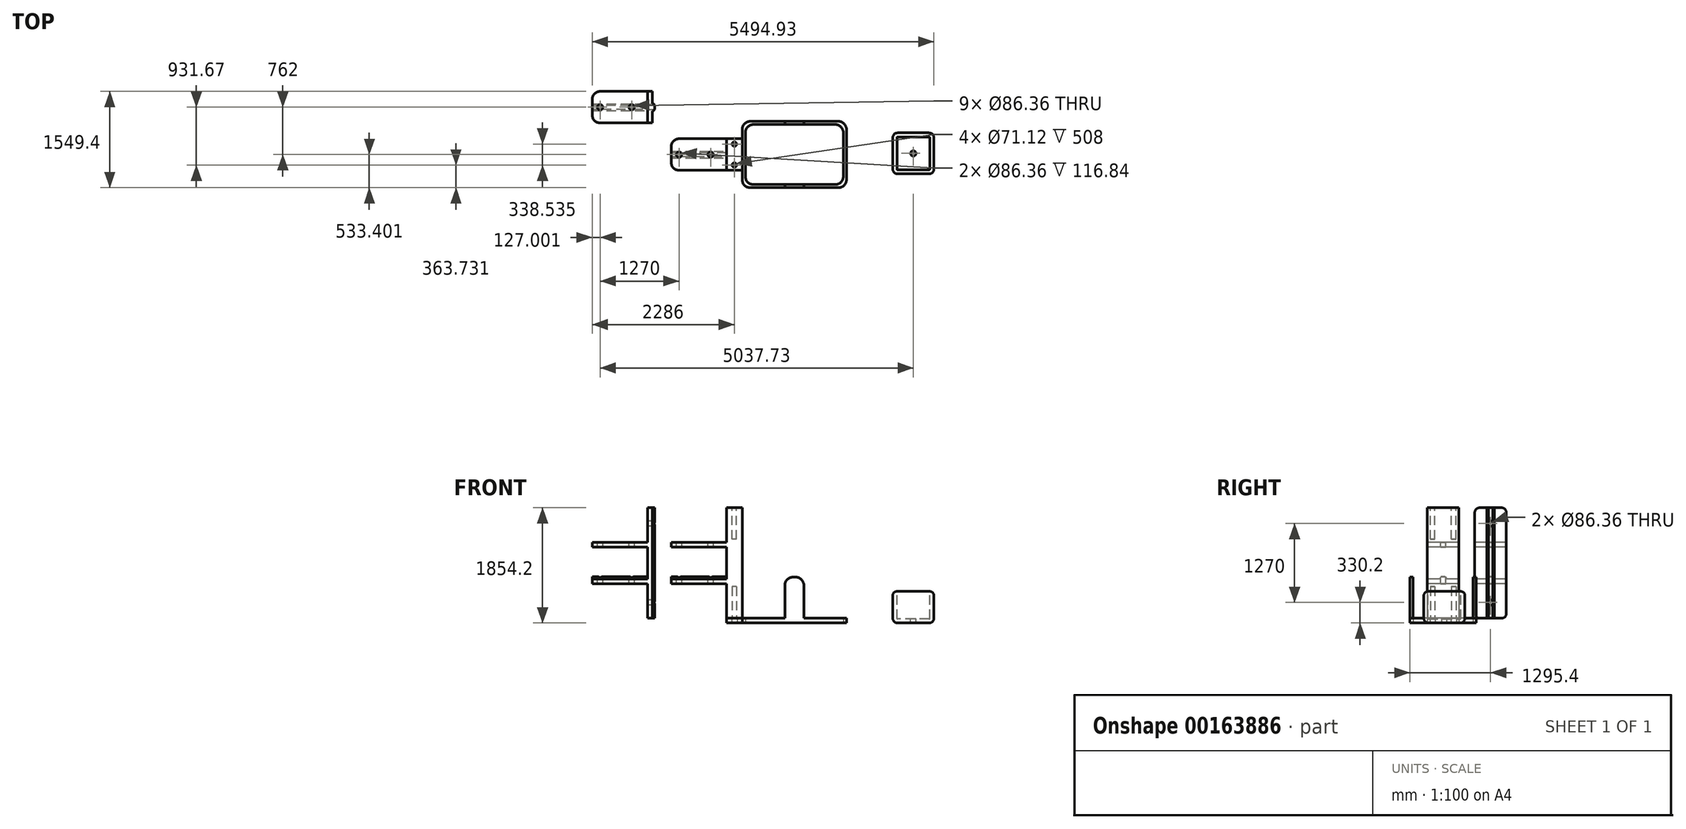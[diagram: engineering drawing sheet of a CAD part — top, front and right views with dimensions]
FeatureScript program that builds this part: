
annotation { "Feature Type Name" : "Feature", "Feature Type Description" : "" }
export const myFeature = defineFeature(function(context is Context, id is Id, definition is map)
    precondition{}
    {
        {
            var Q0;
            Q0=qCreatedBy(makeId("Top.planeOp"),FACE);
            var sketch = newSketch(context, id + "F0", { "sketchPlane" : qUnion([Q0])});
            skLineSegment(sketch, "E0.bottom", {"start": v(-476.12, 579.27) * mm, "end": v(844.68, 579.27) * mm});
            skLineSegment(sketch, "E0.top", {"start": v(-476.12, -385.93) * mm, "end": v(844.68, -385.93) * mm});
            skLineSegment(sketch, "E0.left", {"start": v(-603.12, 452.27) * mm, "end": v(-603.12, -258.93) * mm});
            skLineSegment(sketch, "E0.right", {"start": v(971.68, 452.27) * mm, "end": v(971.68, -258.93) * mm});
            skLineSegment(sketch, "E1.bottom", {"start": v(-526.92, 630.07) * mm, "end": v(895.48, 630.07) * mm});
            skLineSegment(sketch, "E1.top", {"start": v(-526.92, -436.73) * mm, "end": v(895.48, -436.73) * mm});
            skLineSegment(sketch, "E1.left", {"start": v(-653.92, 503.07) * mm, "end": v(-653.92, -309.73) * mm});
            skLineSegment(sketch, "E1.right", {"start": v(1022.48, 503.07) * mm, "end": v(1022.48, -309.73) * mm});
            skLineSegment(sketch, "E2.bottom", {"start": v(-653.92, 350.67) * mm, "end": v(-907.92, 350.67) * mm});
            skLineSegment(sketch, "E2.top", {"start": v(-653.92, -157.33) * mm, "end": v(-907.92, -157.33) * mm});
            skLineSegment(sketch, "E2.left", {"start": v(-653.92, 350.67) * mm, "end": v(-653.92, -157.33) * mm});
            skLineSegment(sketch, "E2.right", {"start": v(-907.92, 350.67) * mm, "end": v(-907.92, -157.33) * mm});
            skCircle(sketch, "E3", {"center": v(-780.92, -73) * mm, "radius": 43.18 * mm});
            skPoint(sketch, "E3.centerSnap0", {"position": v(-780.92, -157.33) * mm});
            skCircle(sketch, "E4", {"center": v(-780.92, 265.54) * mm, "radius": 43.18 * mm});
            skPoint(sketch, "E5.visualSharp", {"position": v(-603.12, 579.27) * mm});
            skArc(sketch, "E5.filletArc", {"start": v(-476.12, 579.27) * mm, "mid": v(-565.92, 542.07) * mm, "end": v(-603.12, 452.27) * mm});
            skPoint(sketch, "E6.visualSharp", {"position": v(971.68, 579.27) * mm});
            skArc(sketch, "E6.filletArc", {"start": v(971.68, 452.27) * mm, "mid": v(934.48, 542.07) * mm, "end": v(844.68, 579.27) * mm});
            skPoint(sketch, "E7.visualSharp", {"position": v(971.68, -385.93) * mm});
            skArc(sketch, "E7.filletArc", {"start": v(844.68, -385.93) * mm, "mid": v(934.48, -348.73) * mm, "end": v(971.68, -258.93) * mm});
            skPoint(sketch, "E8.visualSharp", {"position": v(-603.12, -385.93) * mm});
            skArc(sketch, "E8.filletArc", {"start": v(-603.12, -258.93) * mm, "mid": v(-565.92, -348.73) * mm, "end": v(-476.12, -385.93) * mm});
            skPoint(sketch, "E9.visualSharp", {"position": v(-653.92, -436.73) * mm});
            skArc(sketch, "E9.filletArc", {"start": v(-653.92, -309.73) * mm, "mid": v(-616.72, -399.53) * mm, "end": v(-526.92, -436.73) * mm});
            skPoint(sketch, "E10.visualSharp", {"position": v(1022.48, -436.73) * mm});
            skArc(sketch, "E10.filletArc", {"start": v(895.48, -436.73) * mm, "mid": v(985.28, -399.53) * mm, "end": v(1022.48, -309.73) * mm});
            skPoint(sketch, "E11.visualSharp", {"position": v(1022.48, 630.07) * mm});
            skArc(sketch, "E11.filletArc", {"start": v(1022.48, 503.07) * mm, "mid": v(985.28, 592.87) * mm, "end": v(895.48, 630.07) * mm});
            skPoint(sketch, "E12.visualSharp", {"position": v(-653.92, 630.07) * mm});
            skArc(sketch, "E12.filletArc", {"start": v(-526.92, 630.07) * mm, "mid": v(-616.72, 592.87) * mm, "end": v(-653.92, 503.07) * mm});
            skLineSegment(sketch, "E13", {"start": v(31.88, 630.07) * mm, "end": v(31.88, 579.27) * mm});
            skLineSegment(sketch, "E14", {"start": v(336.68, 630.07) * mm, "end": v(336.68, 579.27) * mm});
            skLineSegment(sketch, "E15", {"start": v(336.68, -385.93) * mm, "end": v(336.68, -436.73) * mm});
            skPoint(sketch, "E15.endSnap0", {"position": v(184.28, -436.73) * mm});
            skLineSegment(sketch, "E16", {"start": v(31.88, -385.93) * mm, "end": v(31.88, -436.73) * mm});
            skSolve(sketch);
        }
        {
            var Q0;
            {var subQ0=sQuery(id+"F0.wireOp",EDGE,"E2.bottom");Q0=makeQuery(id+"F0.imprint","IMPRINT",FACE,{"disambiguationData":[TD([[makeQuery(id+"F0.imprint","IMPRINT",EDGE,{"derivedFrom":subQ0}),1.0]])]});}
            var Q1;
            Q1=makeQuery(id+"F0.imprint","IMPRINT",FACE,{"disambiguationData":[TD([[makeQuery(id+"F0.imprint","IMPRINT",EDGE,{"derivedFrom":sQuery(id+"F0.wireOp",EDGE,"E0.left")}),-1.0]])]});
            var Q2;
            Q2=makeQuery(id+"F0.imprint","IMPRINT",FACE,{"disambiguationData":[TD([[makeQuery(id+"F0.imprint","IMPRINT",EDGE,{"derivedFrom":sQuery(id+"F0.wireOp",EDGE,"E0.right")}),1.0]])]});
            extrude(context, id + "F1", {"entities" : qUnion([Q0, Q1, Q2]), "depth" : 76.2 * mm});
        }
        {
            var Q0;
            {var subQ2=sQuery(id+"F0.wireOp",EDGE,"E13");Q0=makeQuery(id+"F0.imprint","IMPRINT",FACE,{"disambiguationData":[TD([[makeQuery(id+"F0.imprint","IMPRINT",EDGE,{"derivedFrom":subQ2}),1.0]])]});}
            var Q1;
            {var subQ0=sQuery(id+"F0.wireOp",EDGE,"E15");Q1=makeQuery(id+"F0.imprint","IMPRINT",FACE,{"disambiguationData":[TD([[makeQuery(id+"F0.imprint","IMPRINT",EDGE,{"derivedFrom":subQ0}),-1.0]])]});}
            extrude(context, id + "F2", {"entities" : qUnion([Q0, Q1]), "operationType" : NewBodyOperationType.ADD, "depth" : 736.6 * mm});
        }
        {
            var Q0;
            Q0=makeQuery(id+"F2.opExtrude","CAP_EDGE",EDGE,{"disambiguationData":[OSD([sQuery(id+"F0.wireOp",EDGE,"E16")])],"isStart":false});
            var Q1;
            Q1=makeQuery(id+"F2.opExtrude","CAP_EDGE",EDGE,{"disambiguationData":[OSD([sQuery(id+"F0.wireOp",EDGE,"E15")])],"isStart":false});
            var Q2;
            Q2=makeQuery(id+"F2.opExtrude","CAP_EDGE",EDGE,{"disambiguationData":[OSD([sQuery(id+"F0.wireOp",EDGE,"E14")])],"isStart":false});
            var Q3;
            Q3=makeQuery(id+"F2.opExtrude","CAP_EDGE",EDGE,{"disambiguationData":[OSD([sQuery(id+"F0.wireOp",EDGE,"E13")])],"isStart":false});
            var Q4;
            Q4=makeQuery(id+"F1.opExtrude","CAP_EDGE",EDGE,{"disambiguationData":[OSD([sQuery(id+"F0.wireOp",EDGE,"E13")])],"isStart":false});
            var Q5;
            Q5=makeQuery(id+"F1.opExtrude","CAP_EDGE",EDGE,{"disambiguationData":[OSD([sQuery(id+"F0.wireOp",EDGE,"E16")])],"isStart":false});
            var Q6;
            Q6=makeQuery(id+"F1.opExtrude","CAP_EDGE",EDGE,{"disambiguationData":[OSD([sQuery(id+"F0.wireOp",EDGE,"E15")])],"isStart":false});
            var Q7;
            Q7=makeQuery(id+"F1.opExtrude","CAP_EDGE",EDGE,{"disambiguationData":[OSD([sQuery(id+"F0.wireOp",EDGE,"E14")])],"isStart":false});
            fillet(context, id + "F3", {"entities" : qUnion([Q0, Q1, Q2, Q3, Q4, Q5, Q6, Q7]), "radius" : 127 * mm, "tangentPropagation" : true, "allowEdgeOverflow" : false});
        }
        {
            var Q0;
            Q0=makeQuery(id+"F1.opExtrude","CAP_FACE",FACE,{"disambiguationData":[OSD([sQuery(id+"F0.wireOp",EDGE,"E0.bottom"),sQuery(id+"F0.wireOp",EDGE,"E0.top"),sQuery(id+"F0.wireOp",EDGE,"E0.left"),sQuery(id+"F0.wireOp",EDGE,"E1.bottom"),sQuery(id+"F0.wireOp",EDGE,"E1.top"),sQuery(id+"F0.wireOp",EDGE,"E1.left"),sQuery(id+"F0.wireOp",EDGE,"E2.bottom"),sQuery(id+"F0.wireOp",EDGE,"E2.top"),sQuery(id+"F0.wireOp",EDGE,"E2.right"),sQuery(id+"F0.wireOp",EDGE,"E3"),sQuery(id+"F0.wireOp",EDGE,"E4"),sQuery(id+"F0.wireOp",EDGE,"E5.filletArc"),sQuery(id+"F0.wireOp",EDGE,"E8.filletArc"),sQuery(id+"F0.wireOp",EDGE,"E9.filletArc"),sQuery(id+"F0.wireOp",EDGE,"E12.filletArc"),sQuery(id+"F0.wireOp",EDGE,"E13"),sQuery(id+"F0.wireOp",EDGE,"E16")])],"isStart":false});
            var sketch = newSketch(context, id + "F4", { "sketchPlane" : qUnion([Q0])});
            skLineSegment(sketch, "E17.bottom", {"start": v(-907.92, 350.67) * mm, "end": v(-653.92, 350.67) * mm});
            skLineSegment(sketch, "E17.top", {"start": v(-907.92, -157.33) * mm, "end": v(-653.92, -157.33) * mm});
            skLineSegment(sketch, "E17.left", {"start": v(-907.92, 350.67) * mm, "end": v(-907.92, -157.33) * mm});
            skLineSegment(sketch, "E17.right", {"start": v(-653.92, 350.67) * mm, "end": v(-653.92, -157.33) * mm});
            skCircle(sketch, "E18", {"center": v(-780.92, 265.54) * mm, "radius": 35.56 * mm});
            skCircle(sketch, "E19", {"center": v(-780.92, -73) * mm, "radius": 35.56 * mm});
            skSolve(sketch);
        }
        {
            var Q0;
            Q0=makeQuery(id+"F4.imprint","IMPRINT",FACE,{"disambiguationData":[TD([[makeQuery(id+"F4.imprint","IMPRINT",EDGE,{"derivedFrom":sQuery(id+"F4.wireOp",EDGE,"E17.bottom")}),1.0]])]});
            var Q1;
            Q1=makeQuery(id+"F4.imprint","IMPRINT",FACE,{"disambiguationData":[TD([[makeQuery(id+"F4.imprint","IMPRINT",EDGE,{"derivedFrom":sQuery(id+"F4.wireOp",EDGE,"E18")}),1.0]])]});
            var Q2;
            Q2=makeQuery(id+"F4.imprint","IMPRINT",FACE,{"disambiguationData":[TD([[makeQuery(id+"F4.imprint","IMPRINT",EDGE,{"derivedFrom":sQuery(id+"F4.wireOp",EDGE,"E19")}),1.0]])]});
            var Q3;
            Q3=makeQuery(id+"F4.imprint","IMPRINT",FACE,{"disambiguationData":[TD([[makeQuery(id+"F4.imprint","IMPRINT",EDGE,{"derivedFrom":sQuery(id+"F4.wireOp",EDGE,"E19")}),-1.0]])]});
            var Q4;
            Q4=makeQuery(id+"F4.imprint","IMPRINT",FACE,{"disambiguationData":[TD([[makeQuery(id+"F4.imprint","IMPRINT",EDGE,{"derivedFrom":sQuery(id+"F4.wireOp",EDGE,"E18")}),-1.0]])]});
            extrude(context, id + "F5", {"entities" : qUnion([Q0, Q1, Q2, Q3, Q4]), "depth" : 1778 * mm});
        }
        {
            var Q0;
            Q0=makeQuery(id+"F4.imprint","IMPRINT",FACE,{"disambiguationData":[TD([[makeQuery(id+"F4.imprint","IMPRINT",EDGE,{"derivedFrom":sQuery(id+"F4.wireOp",EDGE,"E18")}),1.0]])]});
            var Q1;
            Q1=makeQuery(id+"F4.imprint","IMPRINT",FACE,{"disambiguationData":[TD([[makeQuery(id+"F4.imprint","IMPRINT",EDGE,{"derivedFrom":sQuery(id+"F4.wireOp",EDGE,"E19")}),1.0]])]});
            extrude(context, id + "F6", {"entities" : qUnion([Q0, Q1]), "operationType" : NewBodyOperationType.REMOVE, "depth" : 508 * mm});
        }
        {
            var Q0;
            Q0=makeQuery(id+"F5.opExtrude","CAP_FACE",FACE,{"disambiguationData":[OSD([sQuery(id+"F4.wireOp",EDGE,"E17.bottom"),sQuery(id+"F4.wireOp",EDGE,"E17.top"),sQuery(id+"F4.wireOp",EDGE,"E17.left"),sQuery(id+"F4.wireOp",EDGE,"E17.right")])],"isStart":false});
            var sketch = newSketch(context, id + "F7", { "sketchPlane" : qUnion([Q0])});
            skCircle(sketch, "E20", {"center": v(-780.92, -72.16) * mm, "radius": 35.56 * mm});
            skPoint(sketch, "E20.centerSnap0", {"position": v(-780.92, -157.33) * mm});
            skCircle(sketch, "E21", {"center": v(-780.92, 264.88) * mm, "radius": 35.56 * mm});
            skSolve(sketch);
        }
        {
            var Q0;
            Q0=makeQuery(id+"F7.imprint","IMPRINT",FACE,{"disambiguationData":[TD([[makeQuery(id+"F7.imprint","IMPRINT",EDGE,{"derivedFrom":sQuery(id+"F7.wireOp",EDGE,"E21")}),1.0]])]});
            var Q1;
            Q1=makeQuery(id+"F7.imprint","IMPRINT",FACE,{"disambiguationData":[TD([[makeQuery(id+"F7.imprint","IMPRINT",EDGE,{"derivedFrom":sQuery(id+"F7.wireOp",EDGE,"E20")}),1.0]])]});
            extrude(context, id + "F8", {"entities" : qUnion([Q0, Q1]), "operationType" : NewBodyOperationType.REMOVE, "oppositeDirection" : true, "depth" : 508 * mm});
        }
        {
            var Q0;
            Q0=makeQuery(id+"F5.opExtrude","SWEPT_FACE",FACE,{"disambiguationData":[OSD([sQuery(id+"F4.wireOp",EDGE,"E17.left")])]});
            var sketch = newSketch(context, id + "F9", { "sketchPlane" : qUnion([Q0])});
            skLineSegment(sketch, "E22.bottom", {"start": v(-350.67, 706.12) * mm, "end": v(157.33, 706.12) * mm});
            skLineSegment(sketch, "E22.top", {"start": v(-350.67, 629.92) * mm, "end": v(157.33, 629.92) * mm});
            skLineSegment(sketch, "E22.left", {"start": v(-350.67, 706.12) * mm, "end": v(-350.67, 629.92) * mm});
            skLineSegment(sketch, "E22.right", {"start": v(157.33, 706.12) * mm, "end": v(157.33, 629.92) * mm});
            skLineSegment(sketch, "E23.bottom", {"start": v(-350.67, 1224.28) * mm, "end": v(157.33, 1224.28) * mm});
            skLineSegment(sketch, "E23.top", {"start": v(-350.67, 1300.48) * mm, "end": v(157.33, 1300.48) * mm});
            skLineSegment(sketch, "E23.left", {"start": v(-350.67, 1224.28) * mm, "end": v(-350.67, 1300.48) * mm});
            skLineSegment(sketch, "E23.right", {"start": v(157.33, 1224.28) * mm, "end": v(157.33, 1300.48) * mm});
            skSolve(sketch);
        }
        {
            var Q0;
            Q0=makeQuery(id+"F9.imprint","IMPRINT",FACE,{"disambiguationData":[TD([[makeQuery(id+"F9.imprint","IMPRINT",EDGE,{"derivedFrom":sQuery(id+"F9.wireOp",EDGE,"E22.bottom")}),-1.0]])]});
            var Q1;
            Q1=makeQuery(id+"F9.imprint","IMPRINT",FACE,{"disambiguationData":[TD([[makeQuery(id+"F9.imprint","IMPRINT",EDGE,{"derivedFrom":sQuery(id+"F9.wireOp",EDGE,"E23.bottom")}),1.0]])]});
            extrude(context, id + "F10", {"entities" : qUnion([Q0, Q1]), "operationType" : NewBodyOperationType.ADD, "depth" : 889 * mm});
        }
        {
            var Q0;
            Q0=makeQuery(id+"F10.opExtrude","CAP_EDGE",EDGE,{"disambiguationData":[OSD([sQuery(id+"F9.wireOp",EDGE,"E22.top")])],"isStart":true});
            var Q1;
            Q1=makeQuery(id+"F10.opExtrude","CAP_EDGE",EDGE,{"disambiguationData":[OSD([sQuery(id+"F9.wireOp",EDGE,"E23.top")])],"isStart":true});
            var Q2;
            Q2=makeQuery(id+"F10.opExtrude","CAP_EDGE",EDGE,{"disambiguationData":[OSD([sQuery(id+"F9.wireOp",EDGE,"E22.right")])],"isStart":false});
            var Q3;
            Q3=makeQuery(id+"F10.opExtrude","CAP_EDGE",EDGE,{"disambiguationData":[OSD([sQuery(id+"F9.wireOp",EDGE,"E23.right")])],"isStart":false});
            var Q4;
            Q4=makeQuery(id+"F10.opExtrude","CAP_EDGE",EDGE,{"disambiguationData":[OSD([sQuery(id+"F9.wireOp",EDGE,"E23.left")])],"isStart":false});
            var Q5;
            Q5=makeQuery(id+"F10.opExtrude","CAP_EDGE",EDGE,{"disambiguationData":[OSD([sQuery(id+"F9.wireOp",EDGE,"E22.left")])],"isStart":false});
            fillet(context, id + "F11", {"entities" : qUnion([Q0, Q1, Q2, Q3, Q4, Q5]), "radius" : 127 * mm, "tangentPropagation" : true, "allowEdgeOverflow" : false});
        }
        {
            var Q0;
            Q0=makeQuery(id+"F10.opExtrude","SWEPT_FACE",FACE,{"disambiguationData":[OSD([sQuery(id+"F9.wireOp",EDGE,"E23.top")])]});
            var sketch = newSketch(context, id + "F12", { "sketchPlane" : qUnion([Q0])});
            skCircle(sketch, "E24", {"center": v(-1669.92, 96.67) * mm, "radius": 43.18 * mm});
            skPoint(sketch, "E24.centerSnap0", {"position": v(-1796.92, 96.67) * mm});
            skCircle(sketch, "E25", {"center": v(-1161.92, 96.67) * mm, "radius": 43.18 * mm});
            skSolve(sketch);
        }
        {
            var Q0;
            Q0=makeQuery(id+"F12.imprint","IMPRINT",FACE,{"disambiguationData":[TD([[makeQuery(id+"F12.imprint","IMPRINT",EDGE,{"derivedFrom":sQuery(id+"F12.wireOp",EDGE,"E24")}),1.0]])]});
            var Q1;
            Q1=makeQuery(id+"F12.imprint","IMPRINT",FACE,{"disambiguationData":[TD([[makeQuery(id+"F12.imprint","IMPRINT",EDGE,{"derivedFrom":sQuery(id+"F12.wireOp",EDGE,"E25")}),1.0]])]});
            extrude(context, id + "F13", {"entities" : qUnion([Q0, Q1]), "operationType" : NewBodyOperationType.REMOVE, "endBound" : BoundingType.THROUGH_ALL, "oppositeDirection" : true, "depth" : 25.4 * mm});
        }
        {
            var Q0;
            Q0=makeQuery(id+"F10.opExtrude","SWEPT_FACE",FACE,{"disambiguationData":[OSD([sQuery(id+"F9.wireOp",EDGE,"E22.bottom")])]});
            var sketch = newSketch(context, id + "F14", { "sketchPlane" : qUnion([Q0])});
            skLineSegment(sketch, "E26.bottom", {"start": v(-1796.92, 40.8) * mm, "end": v(-907.92, 40.8) * mm});
            skLineSegment(sketch, "E26.top", {"start": v(-1796.92, 152.55) * mm, "end": v(-907.92, 152.55) * mm});
            skLineSegment(sketch, "E26.left", {"start": v(-1796.92, 40.8) * mm, "end": v(-1796.92, 152.55) * mm});
            skLineSegment(sketch, "E26.right", {"start": v(-907.92, 40.8) * mm, "end": v(-907.92, 152.55) * mm});
            skSolve(sketch);
        }
        {
            var Q0;
            Q0=makeQuery(id+"F14.imprint","IMPRINT",FACE,{"disambiguationData":[TD([[makeQuery(id+"F14.imprint","IMPRINT",EDGE,{"derivedFrom":sQuery(id+"F14.wireOp",EDGE,"E26.bottom")}),1.0]])]});
            extrude(context, id + "F15", {"entities" : qUnion([Q0]), "operationType" : NewBodyOperationType.ADD, "depth" : 40.64 * mm});
        }
        {
            var Q0;
            Q0=makeQuery(id+"F15.opExtrude","CAP_EDGE",EDGE,{"disambiguationData":[OSD([sQuery(id+"F14.wireOp",EDGE,"E26.bottom")])],"isStart":false});
            var Q1;
            Q1=makeQuery(id+"F15.opExtrude","CAP_EDGE",EDGE,{"disambiguationData":[OSD([sQuery(id+"F14.wireOp",EDGE,"E26.top")])],"isStart":false});
            chamfer(context, id + "F16", {"entities" : qUnion([Q0, Q1]), "width" : 25.4 * mm, "tangentPropagation" : true});
        }
        {
            var Q0;
            Q0=makeQuery(id+"F5.opExtrude","SWEPT_BODY",BODY,{"disambiguationData":[OSD([sQuery(id+"F4.wireOp",EDGE,"E17.bottom"),sQuery(id+"F4.wireOp",EDGE,"E17.top"),sQuery(id+"F4.wireOp",EDGE,"E17.left"),sQuery(id+"F4.wireOp",EDGE,"E17.right")])]});
            transform(context, id + "F17", {"entities" : qUnion([Q0]), "transformType" : TransformType.TRANSLATION_3D, "dx" : -1270 * mm, "dy" : 762 * mm, "dz" : 0 * mm, "makeCopy" : true});
        }
        {
            var Q0;
            Q0=makeQuery(id+"F17.opPattern","COPY",FACE,{"derivedFrom":makeQuery(id+"F5.opExtrude","SWEPT_FACE",FACE,{"disambiguationData":[OSD([sQuery(id+"F4.wireOp",EDGE,"E17.right")])]}),"instanceName":"1"});
            extrude(context, id + "F18", {"entities" : qUnion([Q0]), "operationType" : NewBodyOperationType.REMOVE, "oppositeDirection" : true, "depth" : 177.8 * mm});
        }
        {
            var Q0;
            Q0=makeQuery(id+"F17.opPattern","COPY",EDGE,{"derivedFrom":makeQuery(id+"F5.opExtrude","CAP_EDGE",EDGE,{"disambiguationData":[OSD([sQuery(id+"F4.wireOp",EDGE,"E17.top")])],"isStart":false}),"instanceName":"1"});
            var Q1;
            Q1=makeQuery(id+"F17.opPattern","COPY",EDGE,{"derivedFrom":makeQuery(id+"F5.opExtrude","CAP_EDGE",EDGE,{"disambiguationData":[OSD([sQuery(id+"F4.wireOp",EDGE,"E17.bottom")])],"isStart":false}),"instanceName":"1"});
            var Q2;
            Q2=makeQuery(id+"F17.opPattern","COPY",EDGE,{"derivedFrom":makeQuery(id+"F5.opExtrude","CAP_EDGE",EDGE,{"disambiguationData":[OSD([sQuery(id+"F4.wireOp",EDGE,"E17.top")])],"isStart":true}),"instanceName":"1"});
            var Q3;
            Q3=makeQuery(id+"F17.opPattern","COPY",EDGE,{"derivedFrom":makeQuery(id+"F5.opExtrude","CAP_EDGE",EDGE,{"disambiguationData":[OSD([sQuery(id+"F4.wireOp",EDGE,"E17.bottom")])],"isStart":true}),"instanceName":"1"});
            fillet(context, id + "F19", {"entities" : qUnion([Q0, Q1, Q2, Q3]), "radius" : 76.2 * mm, "tangentPropagation" : true, "allowEdgeOverflow" : false});
        }
        {
            var Q0;
            Q0=makeQuery(id+"F18.boolean.opBoolean","COPY",FACE,{"derivedFrom":makeQuery(id+"F18.opExtrude","CAP_FACE",FACE,{"disambiguationData":[OSD([sQuery(id+"F4.wireOp",EDGE,"E17.right")])],"isStart":false})});
            var sketch = newSketch(context, id + "F20", { "sketchPlane" : qUnion([Q0])});
            skLineSegment(sketch, "E27.bottom", {"start": v(797.71, 1854.2) * mm, "end": v(919.63, 1854.2) * mm});
            skLineSegment(sketch, "E27.top", {"start": v(797.71, 76.2) * mm, "end": v(919.63, 76.2) * mm});
            skLineSegment(sketch, "E27.left", {"start": v(797.71, 1854.2) * mm, "end": v(797.71, 76.2) * mm});
            skLineSegment(sketch, "E27.right", {"start": v(919.63, 1854.2) * mm, "end": v(919.63, 76.2) * mm});
            skCircle(sketch, "E28", {"center": v(858.67, 1600.2) * mm, "radius": 43.18 * mm});
            skPoint(sketch, "E28.centerSnap0", {"position": v(858.67, 1854.2) * mm});
            skCircle(sketch, "E29", {"center": v(858.67, 330.2) * mm, "radius": 43.18 * mm});
            skSolve(sketch);
        }
        {
            var Q0;
            Q0=makeQuery(id+"F20.imprint","IMPRINT",FACE,{"disambiguationData":[TD([[makeQuery(id+"F20.imprint","IMPRINT",EDGE,{"derivedFrom":sQuery(id+"F20.wireOp",EDGE,"E27.bottom")}),1.0]])]});
            extrude(context, id + "F21", {"entities" : qUnion([Q0]), "operationType" : NewBodyOperationType.ADD, "depth" : 40.64 * mm});
        }
        {
            var Q0;
            Q0=makeQuery(id+"F21.opExtrude","CAP_EDGE",EDGE,{"disambiguationData":[OSD([sQuery(id+"F20.wireOp",EDGE,"E27.right")])],"isStart":false});
            var Q1;
            Q1=makeQuery(id+"F21.opExtrude","CAP_EDGE",EDGE,{"disambiguationData":[OSD([sQuery(id+"F20.wireOp",EDGE,"E27.left")])],"isStart":false});
            chamfer(context, id + "F22", {"entities" : qUnion([Q0, Q1]), "width" : 25.4 * mm, "tangentPropagation" : true});
        }
        {
            var Q0;
            Q0=makeQuery(id+"F20.imprint","IMPRINT",FACE,{"disambiguationData":[TD([[makeQuery(id+"F20.imprint","IMPRINT",EDGE,{"derivedFrom":sQuery(id+"F20.wireOp",EDGE,"E28")}),1.0]])]});
            var Q1;
            Q1=makeQuery(id+"F20.imprint","IMPRINT",FACE,{"disambiguationData":[TD([[makeQuery(id+"F20.imprint","IMPRINT",EDGE,{"derivedFrom":sQuery(id+"F20.wireOp",EDGE,"E29")}),1.0]])]});
            extrude(context, id + "F23", {"entities" : qUnion([Q0, Q1]), "operationType" : NewBodyOperationType.REMOVE, "endBound" : BoundingType.THROUGH_ALL, "oppositeDirection" : true, "depth" : 25.4 * mm});
        }
        {
            var Q0;
            Q0=makeQuery(id+"F0.imprint","IMPRINT",FACE,{"disambiguationData":[TD([[makeQuery(id+"F0.imprint","IMPRINT",EDGE,{"derivedFrom":sQuery(id+"F0.wireOp",EDGE,"E0.left")}),1.0]])]});
            var sketch = newSketch(context, id + "F24", { "sketchPlane" : qUnion([Q0])});
            skLineSegment(sketch, "E30.bottom", {"start": v(2351.8, -214.82) * mm, "end": v(1843.8, -214.82) * mm});
            skLineSegment(sketch, "E30.top", {"start": v(2351.8, 445.58) * mm, "end": v(1843.8, 445.58) * mm});
            skLineSegment(sketch, "E30.left", {"start": v(2428, -138.62) * mm, "end": v(2428, 369.38) * mm});
            skLineSegment(sketch, "E30.right", {"start": v(1767.6, -138.62) * mm, "end": v(1767.6, 369.38) * mm});
            skPoint(sketch, "E31.visualSharp", {"position": v(2428, -214.82) * mm});
            skArc(sketch, "E31.filletArc", {"start": v(2351.8, -214.82) * mm, "mid": v(2405.7, -192.5) * mm, "end": v(2428, -138.62) * mm});
            skPoint(sketch, "E32.visualSharp", {"position": v(1767.6, -214.82) * mm});
            skArc(sketch, "E32.filletArc", {"start": v(1767.6, -138.62) * mm, "mid": v(1789.93, -192.5) * mm, "end": v(1843.8, -214.82) * mm});
            skPoint(sketch, "E33.visualSharp", {"position": v(1767.6, 445.58) * mm});
            skArc(sketch, "E33.filletArc", {"start": v(1843.8, 445.58) * mm, "mid": v(1789.93, 423.26) * mm, "end": v(1767.6, 369.38) * mm});
            skPoint(sketch, "E34.visualSharp", {"position": v(2428, 445.58) * mm});
            skArc(sketch, "E34.filletArc", {"start": v(2428, 369.38) * mm, "mid": v(2405.7, 423.26) * mm, "end": v(2351.8, 445.58) * mm});
            skSolve(sketch);
        }
        {
            var Q0;
            Q0=makeQuery(id+"F24.imprint","IMPRINT",FACE,{"disambiguationData":[TD([[makeQuery(id+"F24.imprint","IMPRINT",EDGE,{"derivedFrom":sQuery(id+"F24.wireOp",EDGE,"E30.bottom")}),-1.0]])]});
            extrude(context, id + "F25", {"entities" : qUnion([Q0]), "depth" : 508 * mm});
        }
        {
            var Q0;
            Q0=makeQuery(id+"F25.opExtrude","CAP_FACE",FACE,{"disambiguationData":[OSD([sQuery(id+"F24.wireOp",EDGE,"E30.bottom"),sQuery(id+"F24.wireOp",EDGE,"E30.top"),sQuery(id+"F24.wireOp",EDGE,"E30.left"),sQuery(id+"F24.wireOp",EDGE,"E30.right"),sQuery(id+"F24.wireOp",EDGE,"E31.filletArc"),sQuery(id+"F24.wireOp",EDGE,"E32.filletArc"),sQuery(id+"F24.wireOp",EDGE,"E33.filletArc"),sQuery(id+"F24.wireOp",EDGE,"E34.filletArc")])],"isStart":false});
            shell(context, id + "F26", {"entities" : qUnion([Q0]), "thickness" : 66.04 * mm});
        }
        {
            var Q0;
            Q0=makeQuery(id+"F25.opExtrude","CAP_FACE",FACE,{"disambiguationData":[OSD([sQuery(id+"F24.wireOp",EDGE,"E30.bottom"),sQuery(id+"F24.wireOp",EDGE,"E30.top"),sQuery(id+"F24.wireOp",EDGE,"E30.left"),sQuery(id+"F24.wireOp",EDGE,"E30.right"),sQuery(id+"F24.wireOp",EDGE,"E31.filletArc"),sQuery(id+"F24.wireOp",EDGE,"E32.filletArc"),sQuery(id+"F24.wireOp",EDGE,"E33.filletArc"),sQuery(id+"F24.wireOp",EDGE,"E34.filletArc")])],"isStart":false});
            var sketch = newSketch(context, id + "F27", { "sketchPlane" : qUnion([Q0])});
            skPoint(sketch, "E35.0", {"position": v(2428, 115.38) * mm});
            skPoint(sketch, "E36.0", {"position": v(2097.8, -214.82) * mm});
            skCircle(sketch, "E37", {"center": v(2097.8, 115.38) * mm, "radius": 43.18 * mm});
            skPoint(sketch, "E37.centerSnap0", {"position": v(2097.8, -148.78) * mm});
            skSolve(sketch);
        }
        {
            var Q0;
            Q0=makeQuery(id+"F27.imprint","IMPRINT",FACE,{"disambiguationData":[TD([[makeQuery(id+"F27.imprint","IMPRINT",EDGE,{"derivedFrom":sQuery(id+"F27.wireOp",EDGE,"E37")}),1.0]])]});
            extrude(context, id + "F28", {"entities" : qUnion([Q0]), "operationType" : NewBodyOperationType.REMOVE, "endBound" : BoundingType.THROUGH_ALL, "oppositeDirection" : true, "depth" : 25.4 * mm});
        }
        {
            var Q0;
            Q0=makeQuery(id+"F25.opExtrude","CAP_EDGE",EDGE,{"disambiguationData":[OSD([sQuery(id+"F24.wireOp",EDGE,"E30.bottom")])],"isStart":true});
            fillet(context, id + "F29", {"entities" : qUnion([Q0]), "radius" : 76.2 * mm, "tangentPropagation" : true, "allowEdgeOverflow" : false});
        }
        {
            var Q0;
            Q0=makeQuery(id+"F25.opExtrude","CAP_EDGE",EDGE,{"disambiguationData":[OSD([sQuery(id+"F24.wireOp",EDGE,"E30.top")])],"isStart":false});
            fillet(context, id + "F30", {"entities" : qUnion([Q0]), "radius" : 63.5 * mm, "tangentPropagation" : true, "allowEdgeOverflow" : false});
        }
    });
